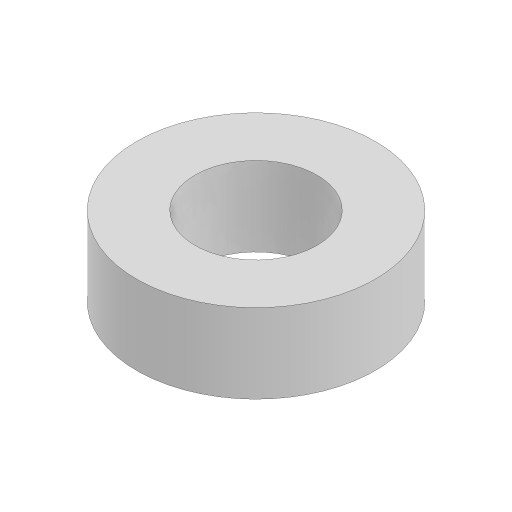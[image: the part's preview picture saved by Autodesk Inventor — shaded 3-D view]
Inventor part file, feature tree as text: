
AUTODESK INVENTOR PART (.ipt)
format: ipt  version: 2024 (Build 280153000, 153)  size: 97,792 bytes
history: native  units: mm
features: extrude x1, direct_edit x1, sketch x1, other x1
ambient origin geometry x8: Origin, YZ Plane, XZ Plane, XY Plane, X Axis, Y Axis, Z Axis, Center Point
bodies: Solid1 (feature_tree)
feature tree (4):
  extrude  "Extrusion1"  Depth=6.35mm
  direct_edit  "Direct Edit1"
  sketch  "Sketch1"  dims[d0=9.525mm d1=4.8mm d2=6.35mm d3=0.0mm d4=-0.127mm]
  other  "Size1"
